# Revit family: Wire-HunterDouglas-Lay_In-Level
name_source: partatom
category: Specialty Equipment
revit_build: Autodesk Revit Architecture 2012 (Build: 20110309_2315(x64)
units: mm (PartAtom-declared; Revit-internal decimal feet)

## types (1)
- Wire Hanger
    04 CSI = 09 51 00
    95 CSI = 09510
    Additional Resources Note = Product details, finishes, construction details, and more can be accessed on the Product Page URL.
    Assembly Code = C3030210
    Default Elevation = 0' - 0"
    Description = Wire Hanger
    EPD URL = In Process
    Fire Rating = Class A
    Flame Spread Index = ≤ 25
    GREENGUARD Certified = Yes
    GREENGUARD URL = http://assets.hunterdouglascontract.com
    HPD URL = In Process
    Hanger Wire Length = 2' - 0"
    High Durability = Yes
    Humidity and Sag Resistant = Yes
    Light Reflectance Average = 1
    Manufacturer = Hunter Douglas Luxalon Metal Ceilings
    Manufacturer Fax = 770-806-0214
    Material = Aluminum
    Model = Wire Hanger
    Mold Resistant = Yes
    Panel Length Range = 24”-120”
    Panel Width Range = 6”-24”
    Perforation Pattern Info URL = http://www.hunterdouglascontract.com
    Product Line = Lay-In Level
    Product Page URL = http://www.hunterdouglascontract.com
    Recyclable = Yes
    Recycled Content Percentage = Min 70%
    Smoke Developed Index = ≤ 50
    Subcategory = Metal – Plank and Tile
    Technical Information = http://assets.hunterdouglascontract.com
    URL = http://www.hunterdouglascontract.com
    VOC Data URL = http://assets.hunterdouglascontract.com
    Wall Angle = Metal - Aluminum Frame - HunterDouglas - Painted White
    Warranty URL = http://assets.hunterdouglascontract.com

## geometry (parser evidence)
native form markers: Sweep x7
no freeform markers — native parametric forms only
